# Revit family: Specialty Equipment_Coat Hook_Metlam_ML415923ab96f4-a329-4f78-be12-ca287680a4ae
name_source: partatom
category: Specialty Equipment
revit_build: Autodesk Revit 2014 (Build: 20130308_1515(x64)
units: mm (PartAtom-declared; Revit-internal decimal feet)

## types (1)
- 19w x 70h x 80d
    Assembly Code = C1030200
    Description = Coat Hook
    Manufacturer = Metlam
    Manufacturer_Overall Depth = 80 mm  [stored 0.262467 ft]
    Manufacturer_Overall Height = 70 mm  [stored 0.229659 ft]
    Manufacturer_Overall Width = 19 mm  [stored 0.062336 ft]
    Manufacturer_Spec Code = ML4159
    Manufacturer_URL__Product Specific = http://www.metlam.com.au
    Material = z_Metlam_Metal_Stainless Steel Satin
    Model = ML4159
    ModifiedIssue_ANZRS = 20150101 $
    Type Comments = ML4159
    URL = www.metlam.com.au

note: [stored X ft] marks values corroborated as IEEE doubles in the binary element streams (Revit-internal decimal feet)

## geometry (parser evidence)
native form markers: Sweep x2
no freeform markers — native parametric forms only
